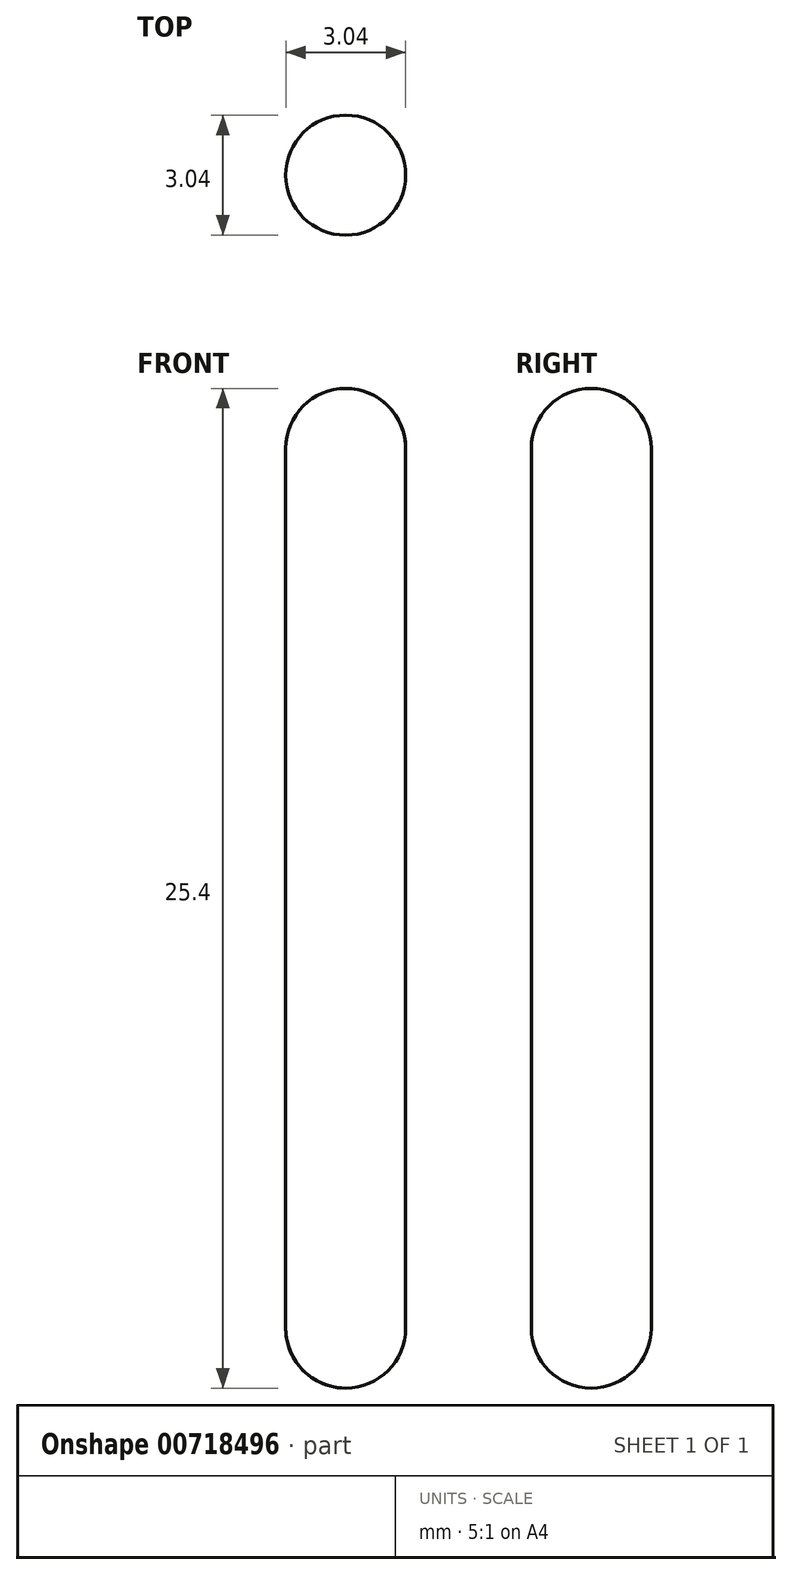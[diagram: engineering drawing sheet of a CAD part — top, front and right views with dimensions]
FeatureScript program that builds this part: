
annotation { "Feature Type Name" : "Feature", "Feature Type Description" : "" }
export const myFeature = defineFeature(function(context is Context, id is Id, definition is map)
    precondition{}
    {
        {
            var Q0;
            Q0=qCreatedBy(makeId("Front.planeOp"),FACE);
            var sketch = newSketch(context, id + "F0", { "sketchPlane" : qUnion([Q0])});
            skArc(sketch, "E0", {"start": v(0, 0) * mm, "mid": v(1.08, 0.45) * mm, "end": v(1.52, 1.52) * mm});
            skLineSegment(sketch, "E1", {"start": v(1.52, 1.52) * mm, "end": v(1.52, 23.88) * mm});
            skArc(sketch, "E2", {"start": v(1.52, 23.88) * mm, "mid": v(1.08, 24.95) * mm, "end": v(0, 25.4) * mm});
            skPoint(sketch, "E3.endSnap0", {"position": v(0, 0) * mm});
            skLineSegment(sketch, "E4", {"start": v(0, 25.4) * mm, "end": v(0, 0) * mm});
            skSolve(sketch);
        }
        {
            var Q0;
            Q0=makeQuery(id+"F0.imprint","IMPRINT",FACE,{"disambiguationData":[TD([[makeQuery(id+"F0.imprint","IMPRINT",EDGE,{"derivedFrom":sQuery(id+"F0.wireOp",EDGE,"E0")}),1.0]])]});
            var Q1;
            Q1=sQuery(id+"F0.wireOp",EDGE,"E4");
            revolve(context, id + "F1", {"surfaceOperationType" : NewSurfaceOperationType.NEW, "entities" : qUnion([Q0]), "axis" : qUnion([Q1]), "revolveType" : RevolveType.FULL});
        }
    });
